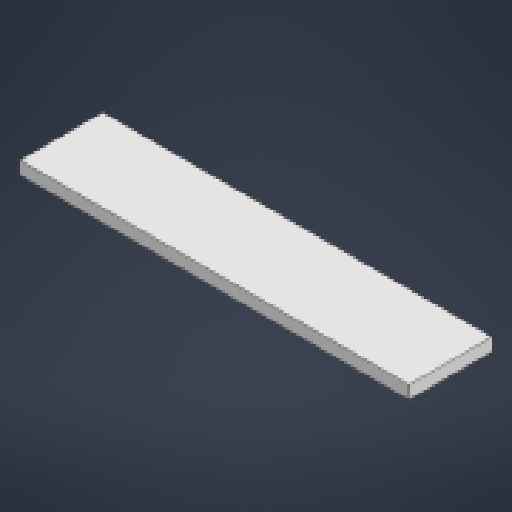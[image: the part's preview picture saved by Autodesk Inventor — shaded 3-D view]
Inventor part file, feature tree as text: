
AUTODESK INVENTOR PART (.ipt)
format: ipt  version: 2024.3 (Build 283343000, 343)  size: 157,696 bytes
history: native  units: mm
features: extrude x1, sketch x1
ambient origin geometry x8: Origin, YZ Plane, XZ Plane, XY Plane, X Axis, Y Axis, Z Axis, Center Point
bodies: Solid1 (feature_tree)
feature tree (2):
  extrude  "Extrusion1"  Depth=31.75mm
  sketch  "Sketch1"  dims[d0=150.0mm d1=31.75mm d2=4.7mm d3=0.0mm]
